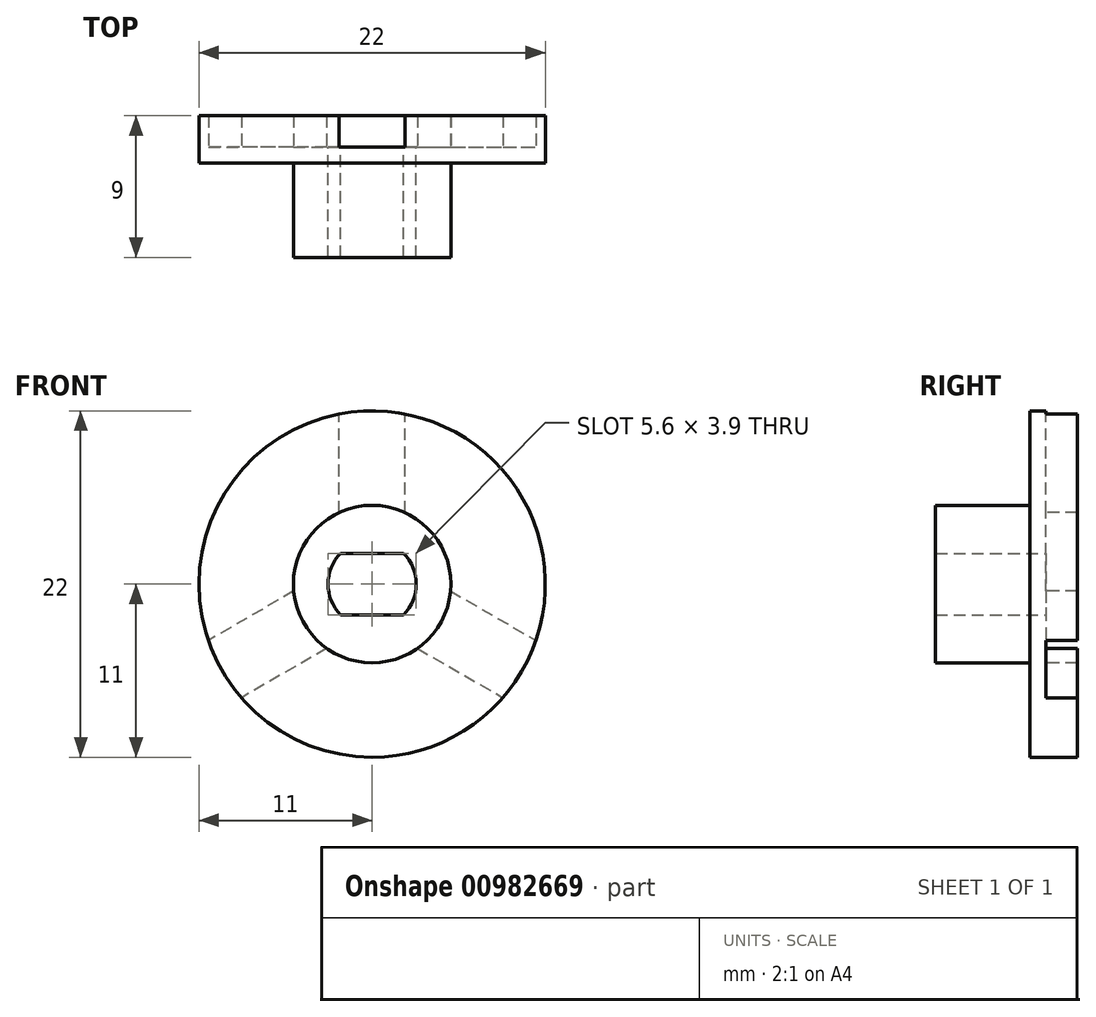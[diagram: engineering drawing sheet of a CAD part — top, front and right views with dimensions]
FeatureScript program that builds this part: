
annotation { "Feature Type Name" : "Feature", "Feature Type Description" : "" }
export const myFeature = defineFeature(function(context is Context, id is Id, definition is map)
    precondition{}
    {
        {
            var Q0;
            Q0=qCreatedBy(makeId("Front.planeOp"),FACE);
            var sketch = newSketch(context, id + "F0", { "sketchPlane" : qUnion([Q0])});
            skArc(sketch, "E0", {"start": v(-2, 1.95) * mm, "mid": v(-2.8, 0) * mm, "end": v(-2, -1.95) * mm});
            skLineSegment(sketch, "E1", {"start": v(-2, 1.95) * mm, "end": v(2, 1.95) * mm});
            skLineSegment(sketch, "E2", {"start": v(2, -1.95) * mm, "end": v(-2, -1.95) * mm});
            skCircle(sketch, "E3", {"center": v(0, 0) * mm, "radius": 11 * mm});
            skArc(sketch, "E4.trimOffspring", {"start": v(2, -1.95) * mm, "mid": v(2.8, 0) * mm, "end": v(2, 1.95) * mm});
            skSolve(sketch);
        }
        {
            var Q0;
            Q0=makeQuery(id+"F0.imprint","IMPRINT",FACE,{"disambiguationData":[TD([[makeQuery(id+"F0.imprint","IMPRINT",EDGE,{"derivedFrom":sQuery(id+"F0.wireOp",EDGE,"E0")}),-1.0]])]});
            extrude(context, id + "F1", {"entities" : qUnion([Q0]), "depth" : 1 * mm, "offsetDistance" : 25 * mm});
        }
        {
            var Q0;
            Q0=makeQuery(id+"F1.opExtrude","CAP_FACE",FACE,{"disambiguationData":[OSD([sQuery(id+"F0.wireOp",EDGE,"E0"),sQuery(id+"F0.wireOp",EDGE,"E1"),sQuery(id+"F0.wireOp",EDGE,"E2"),sQuery(id+"F0.wireOp",EDGE,"E3"),sQuery(id+"F0.wireOp",EDGE,"E4.trimOffspring")])],"isStart":true});
            var sketch = newSketch(context, id + "F2", { "sketchPlane" : qUnion([Q0])});
            skCircle(sketch, "E5", {"center": v(0, 0) * mm, "radius": 5 * mm});
            skLineSegment(sketch, "E6", {"start": v(-2.1, 4.54) * mm, "end": v(-2.1, 10.8) * mm});
            skLineSegment(sketch, "E7", {"start": v(2.1, 4.54) * mm, "end": v(2.1, 10.8) * mm});
            skLineSegment(sketch, "E8", {"start": v(0, 5) * mm, "end": v(0, 11) * mm, "construction": true});
            skLineSegment(sketch, "E9.1.0", {"start": v(-2.88, -4.09) * mm, "end": v(-8.3, -7.22) * mm});
            skLineSegment(sketch, "E9.1.1", {"start": v(-4.98, -0.45) * mm, "end": v(-10.4, -3.58) * mm});
            skLineSegment(sketch, "E9.2.0", {"start": v(4.98, -0.45) * mm, "end": v(10.4, -3.58) * mm});
            skLineSegment(sketch, "E9.2.1", {"start": v(2.88, -4.09) * mm, "end": v(8.3, -7.22) * mm});
            skSolve(sketch);
        }
        {
            var Q0;
            {var subQ0=sQuery(id+"F2.wireOp",EDGE,"E6");Q0=makeQuery(id+"F2.imprint","IMPRINT",FACE,{"disambiguationData":[TD([[makeQuery(id+"F2.imprint","IMPRINT",EDGE,{"derivedFrom":subQ0}),1.0]])]});}
            var Q1;
            {var subQ0=sQuery(id+"F2.wireOp",EDGE,"E7");Q1=makeQuery(id+"F2.imprint","IMPRINT",FACE,{"disambiguationData":[TD([[makeQuery(id+"F2.imprint","IMPRINT",EDGE,{"derivedFrom":subQ0}),-1.0]])]});}
            var Q2;
            {var subQ0=sQuery(id+"F2.wireOp",EDGE,"E9.1.0");Q2=makeQuery(id+"F2.imprint","IMPRINT",FACE,{"disambiguationData":[TD([[makeQuery(id+"F2.imprint","IMPRINT",EDGE,{"derivedFrom":subQ0}),1.0]])]});}
            extrude(context, id + "F3", {"entities" : qUnion([Q0, Q1, Q2]), "operationType" : NewBodyOperationType.ADD, "depth" : 2 * mm, "offsetDistance" : 25 * mm});
        }
        {
            var Q0;
            Q0=makeQuery(id+"F1.opExtrude","CAP_FACE",FACE,{"disambiguationData":[OSD([sQuery(id+"F0.wireOp",EDGE,"E0"),sQuery(id+"F0.wireOp",EDGE,"E1"),sQuery(id+"F0.wireOp",EDGE,"E2"),sQuery(id+"F0.wireOp",EDGE,"E3"),sQuery(id+"F0.wireOp",EDGE,"E4.trimOffspring")])],"isStart":false});
            var sketch = newSketch(context, id + "F4", { "sketchPlane" : qUnion([Q0])});
            skCircle(sketch, "E10", {"center": v(0, 0) * mm, "radius": 5 * mm});
            skLineSegment(sketch, "E11.0", {"start": v(2, -1.95) * mm, "end": v(-2, -1.95) * mm});
            skArc(sketch, "E11.1", {"start": v(-2, 1.95) * mm, "mid": v(-2.8, 0) * mm, "end": v(-2, -1.95) * mm});
            skLineSegment(sketch, "E11.2", {"start": v(-2, 1.95) * mm, "end": v(2, 1.95) * mm});
            skArc(sketch, "E11.3", {"start": v(2, -1.95) * mm, "mid": v(2.8, 0) * mm, "end": v(2, 1.95) * mm});
            skSolve(sketch);
        }
        {
            var Q0;
            Q0 = qSketchRegion(id + "F4", true);
            extrude(context, id + "F5", {"entities" : qUnion([Q0]), "operationType" : NewBodyOperationType.ADD, "depth" : 6 * mm, "offsetDistance" : 25 * mm});
        }
    });
